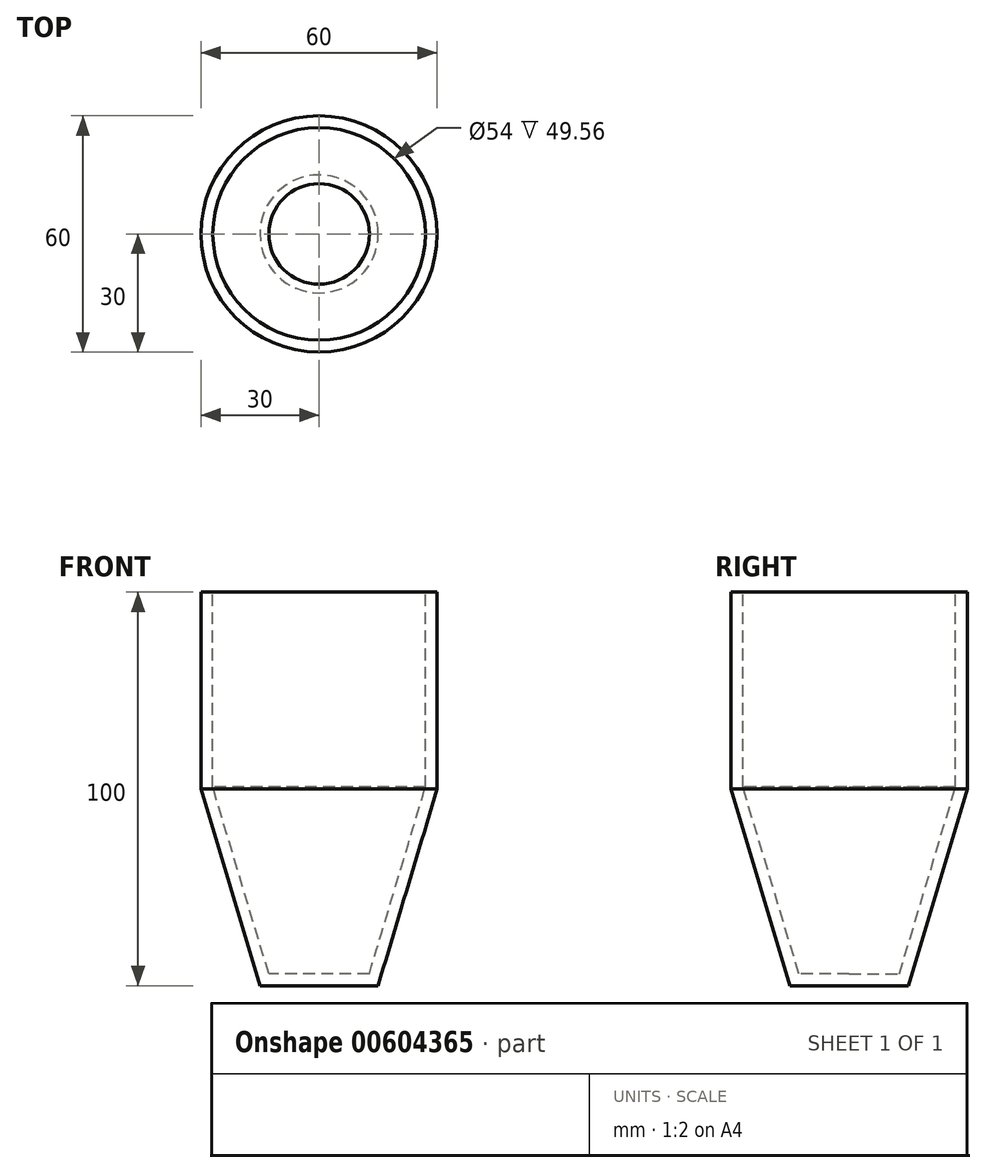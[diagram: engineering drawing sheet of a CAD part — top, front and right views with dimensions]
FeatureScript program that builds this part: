
annotation { "Feature Type Name" : "Feature", "Feature Type Description" : "" }
export const myFeature = defineFeature(function(context is Context, id is Id, definition is map)
    precondition{}
    {
        {
            var Q0;
            Q0=qCreatedBy(makeId("Front.planeOp"),FACE);
            var sketch = newSketch(context, id + "F0", { "sketchPlane" : qUnion([Q0])});
            skLineSegment(sketch, "E0", {"start": v(0, 100) * mm, "end": v(-30, 100) * mm});
            skLineSegment(sketch, "E1", {"start": v(-30, 100) * mm, "end": v(-30, 50) * mm});
            skLineSegment(sketch, "E2", {"start": v(-30, 50) * mm, "end": v(-15, 0) * mm});
            skLineSegment(sketch, "E3", {"start": v(-15, 0) * mm, "end": v(0, 0) * mm});
            skPoint(sketch, "E4.endSnap0", {"position": v(-7.5, 0) * mm});
            skLineSegment(sketch, "E5", {"start": v(0, 0) * mm, "end": v(-15, 0) * mm});
            skLineSegment(sketch, "E6", {"start": v(0, 100) * mm, "end": v(0, 0) * mm});
            skLineSegment(sketch, "E7", {"start": v(0, 145.54) * mm, "end": v(0, -34.7) * mm, "construction": true});
            skSolve(sketch);
        }
        {
            var Q0;
            Q0=makeQuery(id+"F0.imprint","IMPRINT",FACE,{"disambiguationData":[TD([[makeQuery(id+"F0.imprint","IMPRINT",EDGE,{"derivedFrom":sQuery(id+"F0.wireOp",EDGE,"E0")}),1.0]])]});
            var Q1;
            Q1=sQuery(id+"F0.wireOp",EDGE,"E6");
            revolve(context, id + "F1", {"entities" : qUnion([Q0]), "axis" : qUnion([Q1]), "revolveType" : RevolveType.FULL});
        }
        {
            var Q0;
            Q0=makeQuery(id+"F1.opRevolve","SWEPT_FACE",FACE,{"disambiguationData":[OSD([sQuery(id+"F0.wireOp",EDGE,"E0")])]});
            var Q1;
            Q1=makeQuery(id+"F1.opRevolve","SWEPT_FACE",FACE,{"disambiguationData":[OSD([sQuery(id+"F0.wireOp",EDGE,"E5")])]});
            shell(context, id + "F2", {"entities" : qUnion([Q0, Q1]), "thickness" : 3 * mm});
        }
    });
